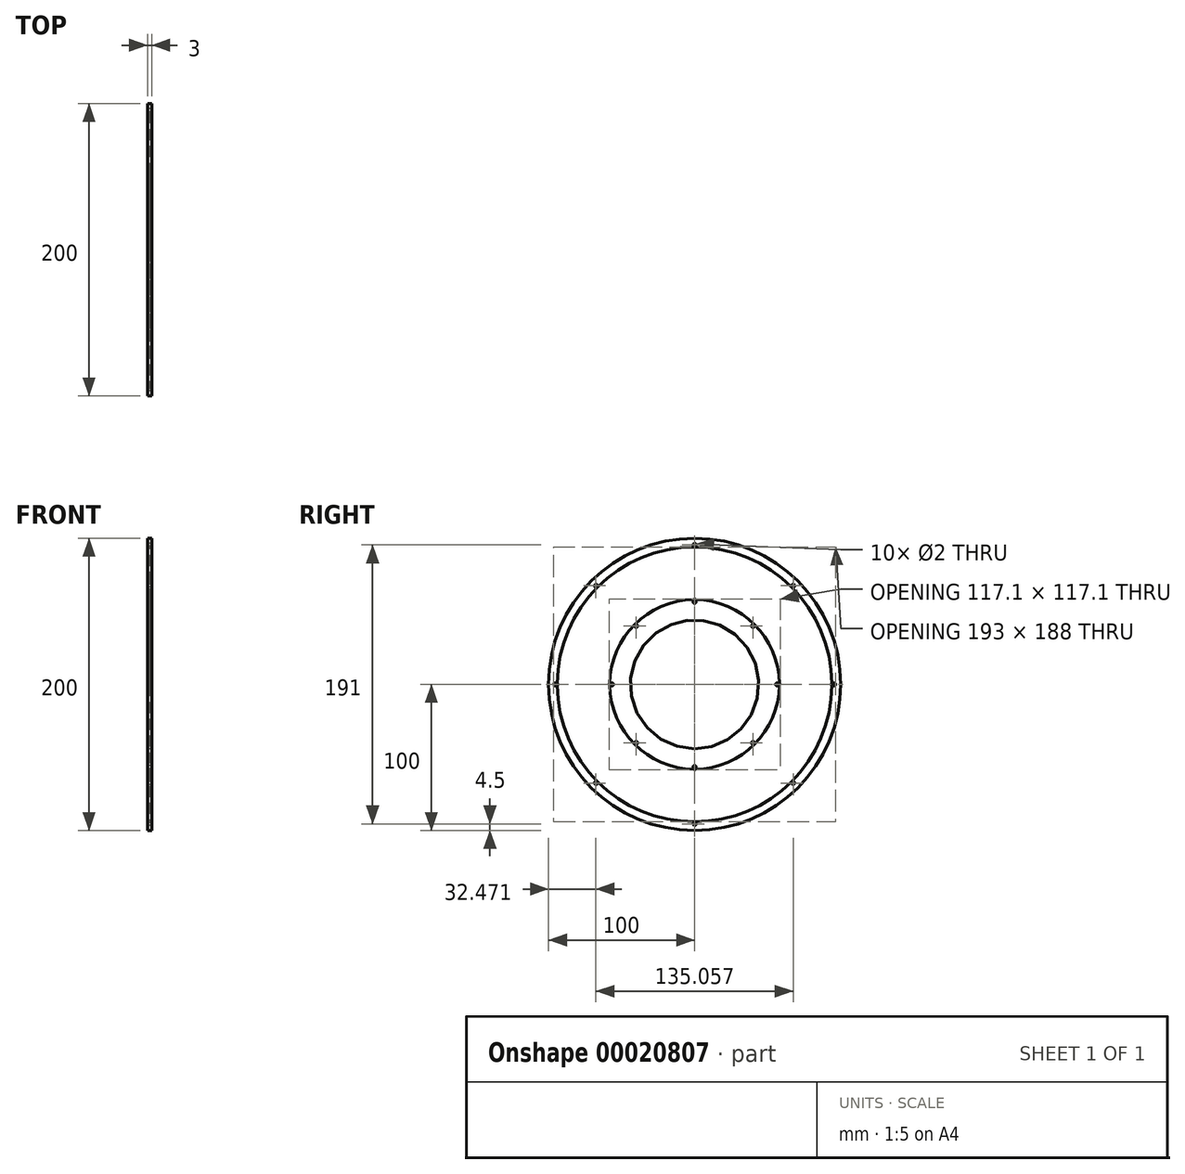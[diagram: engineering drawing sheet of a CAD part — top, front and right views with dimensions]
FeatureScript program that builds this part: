
annotation { "Feature Type Name" : "Feature", "Feature Type Description" : "" }
export const myFeature = defineFeature(function(context is Context, id is Id, definition is map)
    precondition{}
    {
        {
            var Q0;
            Q0=qCreatedBy(makeId("Right.planeOp"),FACE);
            var sketch = newSketch(context, id + "F0", { "sketchPlane" : qUnion([Q0])});
            skCircle(sketch, "E0", {"center": v(0, 0) * mm, "radius": 44 * mm});
            skCircle(sketch, "E1", {"center": v(0, 0) * mm, "radius": 58 * mm});
            skCircle(sketch, "E2", {"center": v(0, 0) * mm, "radius": 100 * mm});
            skCircle(sketch, "E3", {"center": v(0, 0) * mm, "radius": 94 * mm});
            skCircle(sketch, "E4", {"center": v(95.5, 0) * mm, "radius": 1 * mm});
            skCircle(sketch, "E5", {"center": v(56.5, 0) * mm, "radius": 1 * mm});
            skCircle(sketch, "E6.1.0", {"center": v(67.53, 67.53) * mm, "radius": 1 * mm});
            skCircle(sketch, "E6.1.1", {"center": v(39.95, 39.95) * mm, "radius": 1 * mm});
            skCircle(sketch, "E6.2.0", {"center": v(0, 95.5) * mm, "radius": 1 * mm});
            skCircle(sketch, "E6.2.1", {"center": v(0, 56.5) * mm, "radius": 1 * mm});
            skCircle(sketch, "E6.3.0", {"center": v(-67.53, 67.53) * mm, "radius": 1 * mm});
            skCircle(sketch, "E6.3.1", {"center": v(-39.95, 39.95) * mm, "radius": 1 * mm});
            skCircle(sketch, "E6.4.0", {"center": v(-95.5, 0) * mm, "radius": 1 * mm});
            skCircle(sketch, "E6.4.1", {"center": v(-56.5, 0) * mm, "radius": 1 * mm});
            skCircle(sketch, "E6.5.0", {"center": v(-67.53, -67.53) * mm, "radius": 1 * mm});
            skCircle(sketch, "E6.5.1", {"center": v(-39.95, -39.95) * mm, "radius": 1 * mm});
            skCircle(sketch, "E6.6.0", {"center": v(0, -95.5) * mm, "radius": 1 * mm});
            skCircle(sketch, "E6.6.1", {"center": v(0, -56.5) * mm, "radius": 1 * mm});
            skCircle(sketch, "E6.7.0", {"center": v(67.53, -67.53) * mm, "radius": 1 * mm});
            skCircle(sketch, "E6.7.1", {"center": v(39.95, -39.95) * mm, "radius": 1 * mm});
            skPoint(sketch, "E7", {"position": v(-94, 0) * mm});
            skPoint(sketch, "E8", {"position": v(-58, 0) * mm});
            skPoint(sketch, "E9", {"position": v(0, -58) * mm});
            skPoint(sketch, "E10", {"position": v(0, 58) * mm});
            skPoint(sketch, "E11", {"position": v(58, 0) * mm});
            skPoint(sketch, "E12", {"position": v(94, 0) * mm});
            skSolve(sketch);
        }
        {
            var Q0;
            Q0=makeQuery(id+"F0.imprint","IMPRINT",FACE,{"disambiguationData":[TD([[makeQuery(id+"F0.imprint","IMPRINT",EDGE,{"derivedFrom":sQuery(id+"F0.wireOp",EDGE,"E2")}),1.0]])]});
            var Q1;
            Q1=makeQuery(id+"F0.imprint","IMPRINT",FACE,{"disambiguationData":[TD([[makeQuery(id+"F0.imprint","IMPRINT",EDGE,{"derivedFrom":sQuery(id+"F0.wireOp",EDGE,"E0")}),-1.0]])]});
            extrude(context, id + "F1", {"entities" : qUnion([Q0, Q1]), "depth" : 1 * mm});
        }
        {
            var Q0;
            Q0=makeQuery(id+"F0.imprint","IMPRINT",FACE,{"disambiguationData":[TD([[makeQuery(id+"F0.imprint","IMPRINT",EDGE,{"derivedFrom":sQuery(id+"F0.wireOp",EDGE,"E1")}),-1.0]])]});
            var Q1;
            Q1=makeQuery(id+"F0.imprint","IMPRINT",FACE,{"disambiguationData":[TD([[makeQuery(id+"F0.imprint","IMPRINT",EDGE,{"derivedFrom":sQuery(id+"F0.wireOp",EDGE,"E0")}),-1.0]])]});
            var Q2;
            Q2=makeQuery(id+"F0.imprint","IMPRINT",FACE,{"disambiguationData":[TD([[makeQuery(id+"F0.imprint","IMPRINT",EDGE,{"derivedFrom":sQuery(id+"F0.wireOp",EDGE,"E2")}),1.0]])]});
            extrude(context, id + "F2", {"entities" : qUnion([Q0, Q1, Q2]), "operationType" : NewBodyOperationType.ADD, "oppositeDirection" : true, "depth" : 1 * mm});
        }
        {
            var Q0;
            Q0=makeQuery(id+"F0.imprint","IMPRINT",FACE,{"disambiguationData":[TD([[makeQuery(id+"F0.imprint","IMPRINT",EDGE,{"derivedFrom":sQuery(id+"F0.wireOp",EDGE,"E2")}),1.0]])]});
            var Q1;
            Q1=makeQuery(id+"F0.imprint","IMPRINT",FACE,{"disambiguationData":[TD([[makeQuery(id+"F0.imprint","IMPRINT",EDGE,{"derivedFrom":sQuery(id+"F0.wireOp",EDGE,"E0")}),-1.0]])]});
            extrude(context, id + "F3", {"entities" : qUnion([Q0, Q1]), "operationType" : NewBodyOperationType.ADD, "oppositeDirection" : true, "depth" : 2 * mm});
        }
        {
            var Q0;
            Q0=sQuery(id+"F0.wireOp",VERTEX,"E12");
            var Q1;
            Q1=sQuery(id+"F0.wireOp",VERTEX,"E8");
            var Q2;
            Q2=sQuery(id+"F0.wireOp",VERTEX,"E7");
            var Q3;
            Q3=sQuery(id+"F0.wireOp",VERTEX,"E10");
            var Q4;
            Q4=sQuery(id+"F0.wireOp",VERTEX,"E11");
            var Q5;
            Q5=sQuery(id+"F0.wireOp",VERTEX,"E9");
            var Q6;
            Q6=makeQuery(id+"F1.opExtrude","SWEPT_BODY",BODY,{"disambiguationData":[OSD([sQuery(id+"F0.wireOp",EDGE,"E0"),sQuery(id+"F0.wireOp",EDGE,"E1"),sQuery(id+"F0.wireOp",EDGE,"E5"),sQuery(id+"F0.wireOp",EDGE,"E6.1.1"),sQuery(id+"F0.wireOp",EDGE,"E6.2.1"),sQuery(id+"F0.wireOp",EDGE,"E6.3.1"),sQuery(id+"F0.wireOp",EDGE,"E6.4.1"),sQuery(id+"F0.wireOp",EDGE,"E6.5.1"),sQuery(id+"F0.wireOp",EDGE,"E6.6.1"),sQuery(id+"F0.wireOp",EDGE,"E6.7.1")])]});
            hole(context, id + "F4", {"style" : HoleStyle.SIMPLE, "holeDiameter" : 1.1 * mm, "endStyle" : HoleEndStyle.THROUGH, "locations" : qUnion([Q0, Q1, Q2, Q3, Q4, Q5]), "scope" : qUnion([Q6])});
        }
        {
            var Q0;
            Q0=sQuery(id+"F0.wireOp",VERTEX,"E7");
            var Q1;
            Q1=sQuery(id+"F0.wireOp",VERTEX,"E8");
            var Q2;
            Q2=sQuery(id+"F0.wireOp",VERTEX,"E9");
            var Q3;
            Q3=sQuery(id+"F0.wireOp",VERTEX,"E12");
            var Q4;
            Q4=sQuery(id+"F0.wireOp",VERTEX,"E11");
            var Q5;
            Q5=sQuery(id+"F0.wireOp",VERTEX,"E10");
            var Q6;
            Q6=makeQuery(id+"F1.opExtrude","SWEPT_BODY",BODY,{"disambiguationData":[OSD([sQuery(id+"F0.wireOp",EDGE,"E0"),sQuery(id+"F0.wireOp",EDGE,"E1"),sQuery(id+"F0.wireOp",EDGE,"E5"),sQuery(id+"F0.wireOp",EDGE,"E6.1.1"),sQuery(id+"F0.wireOp",EDGE,"E6.2.1"),sQuery(id+"F0.wireOp",EDGE,"E6.3.1"),sQuery(id+"F0.wireOp",EDGE,"E6.4.1"),sQuery(id+"F0.wireOp",EDGE,"E6.5.1"),sQuery(id+"F0.wireOp",EDGE,"E6.6.1"),sQuery(id+"F0.wireOp",EDGE,"E6.7.1")])]});
            hole(context, id + "F5", {"style" : HoleStyle.SIMPLE, "holeDiameter" : 1.1 * mm, "endStyle" : HoleEndStyle.THROUGH, "oppositeDirection" : true, "locations" : qUnion([Q0, Q1, Q2, Q3, Q4, Q5]), "scope" : qUnion([Q6])});
        }
        {
            var Q0;
            Q0=makeQuery(id+"F3.opExtrude","CAP_EDGE",EDGE,{"disambiguationData":[OSD([sQuery(id+"F0.wireOp",EDGE,"E0")])],"isStart":false});
            var Q1;
            Q1=makeQuery(id+"F1.opExtrude","CAP_EDGE",EDGE,{"disambiguationData":[OSD([sQuery(id+"F0.wireOp",EDGE,"E0")])],"isStart":false});
            fillet(context, id + "F6", {"entities" : qUnion([Q0, Q1]), "radius" : 1.5 * mm, "tangentPropagation" : true, "allowEdgeOverflow" : false});
        }
    });
